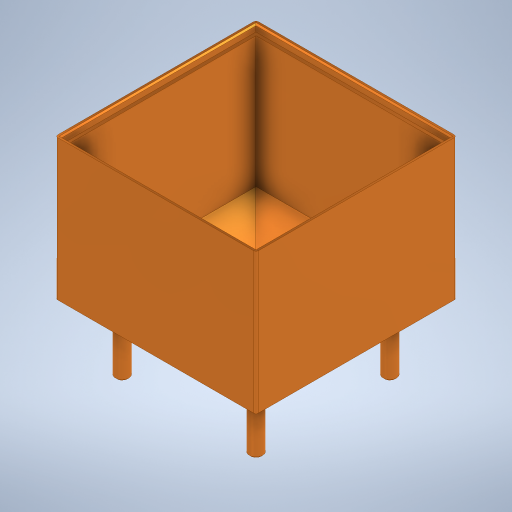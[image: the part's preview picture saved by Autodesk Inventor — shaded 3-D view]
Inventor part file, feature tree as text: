
AUTODESK INVENTOR PART (.ipt)
format: ipt  version: 2023 (Build 270158000, 158)  size: 399,360 bytes
history: native  units: mm
features: sketch x7, extrude x5, chamfer x2, plane x1, loft x1, shell x1, hole x1, fillet x1, other x1
ambient origin geometry x8: Origin, YZ Plane, XZ Plane, XY Plane, X Axis, Y Axis, Z Axis, Center Point
bodies: Solid1 (feature_tree)
feature tree (20):
  extrude  "Extrusion1"  Depth=150.0mm
  extrude  "Extrusion2"  Depth=75.0mm
  plane  "Work Plane1"
  loft  "Loft1"
  shell  "Shell2"  Thickness=140.0mm
  hole  "Hole1"  [1 undecoded]
  extrude  "Extrusion3"  Depth=50.0mm
  extrude  "Extrusion4"  TaperAngle=0.0deg  [1 undecoded]
  chamfer  "Chamfer1"  Angle=90.0deg  [1 undecoded]
  extrude  "Extrusion5"  Depth=2.0mm TaperAngle=0.0deg
  chamfer  "Chamfer2"  Distance=2.5mm
  fillet  "Fillet1"  Radius=2.5mm
  sketch  "Sketch1"  dims[d0=150.0mm d1=150.0mm]
  sketch  "Sketch2"  dims[d4=100.0mm d5=0.0mm d6=75.0mm]
  sketch  "Sketch3"  dims[d7=75.0mm d8=140.0mm d9=140.0mm]
  other  "Edges1"
  sketch  "Sketch6"  dims[d10=5.0mm d11=5.0mm]
  sketch  "Sketch8"  dims[d12=90.0mm d13=0.0mm d14=50.0mm]
  sketch  "Sketch9"  dims[d15=30.0mm d16=0.0mm d17=90.0deg d18=0.0mm d19=90.0deg]
  sketch  "Sketch10"  dims[d21=5.0mm d22=50.0mm d23=6.0mm d24=4.0mm d25=2.0mm d26=90.0deg d27=8.0mm d28=20.594885mm d29=5.0mm d30=0.0mm d31=2.5mm d32=2.5mm d33=5.0mm d34=0.0mm d35=1.0mm d36=2.0mm d37=45.0deg d38=10.0mm d39=50.0mm d40=10.0mm d41=10.0mm d42=10.0mm d43=0.0mm d44=0.0mm d45=1.0mm d46=2.0mm d47=45.0deg d48=2.0mm d49=0.375mm]
note: 3 required parameter values undecoded (feature->parameter linkage not recoverable at this tier; creation-order binding heuristic only, values carry confidence <= 0.55)
